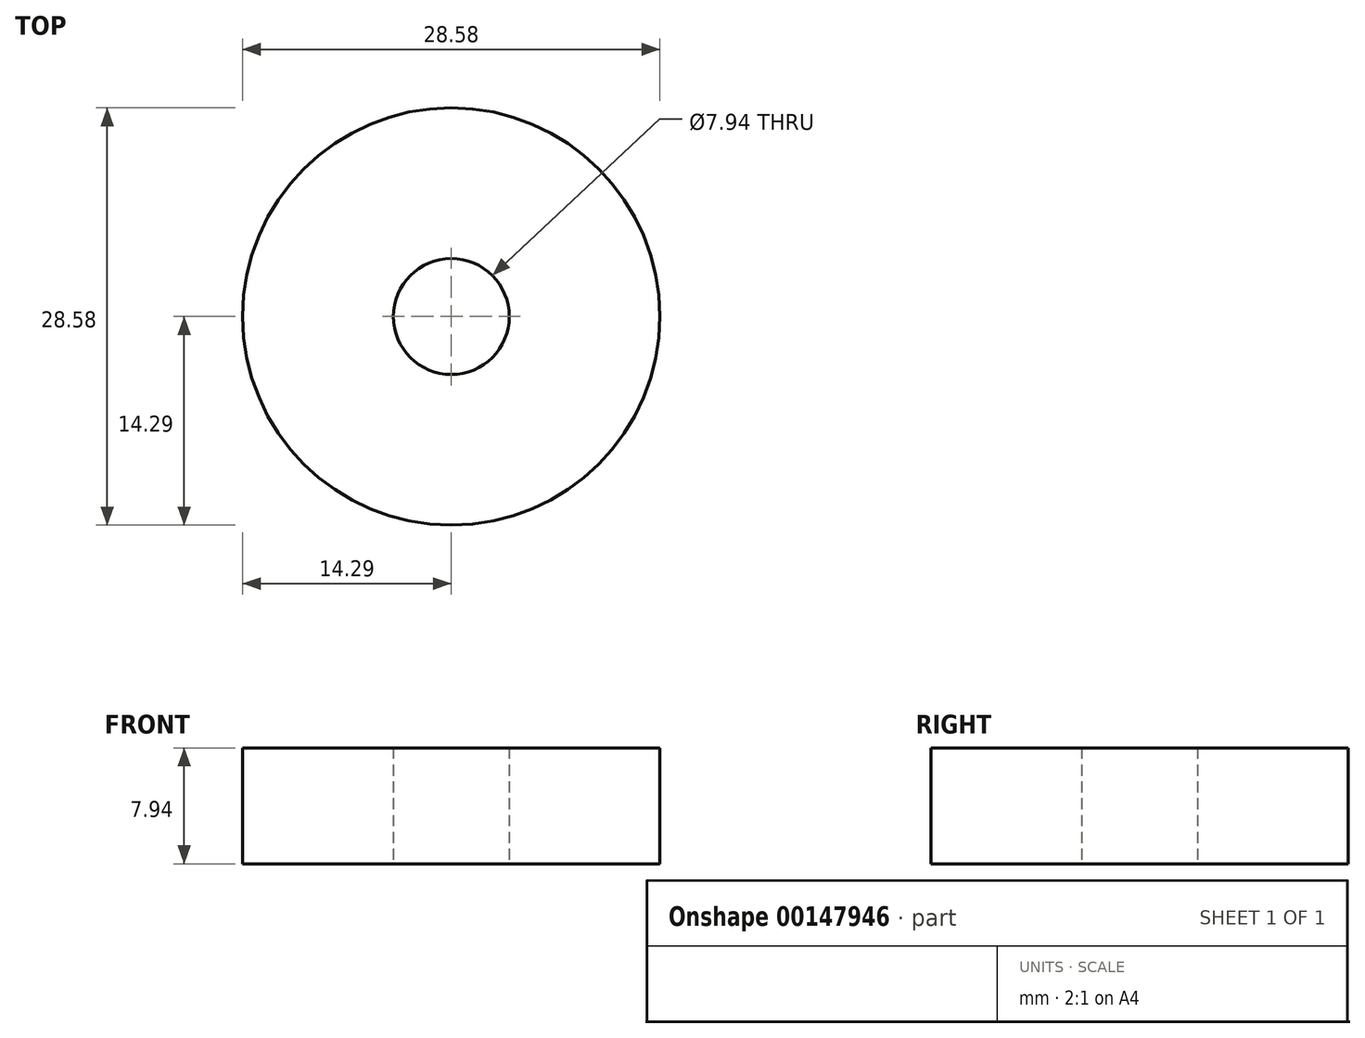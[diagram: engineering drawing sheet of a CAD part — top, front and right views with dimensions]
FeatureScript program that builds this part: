
annotation { "Feature Type Name" : "Feature", "Feature Type Description" : "" }
export const myFeature = defineFeature(function(context is Context, id is Id, definition is map)
    precondition{}
    {
        {
            var Q0;
            Q0=qCreatedBy(makeId("Top.planeOp"),FACE);
            var sketch = newSketch(context, id + "F0", { "sketchPlane" : qUnion([Q0])});
            skCircle(sketch, "E0", {"center": v(0, 0) * mm, "radius": 14.29 * mm});
            skCircle(sketch, "E1", {"center": v(0, 0) * mm, "radius": 3.97 * mm});
            skSolve(sketch);
        }
        {
            var Q0;
            Q0=qSketchRegion(id+"F0",true);
            extrude(context, id + "F1", {"entities" : qUnion([Q0]), "depth" : 7.94 * mm});
        }
    });
